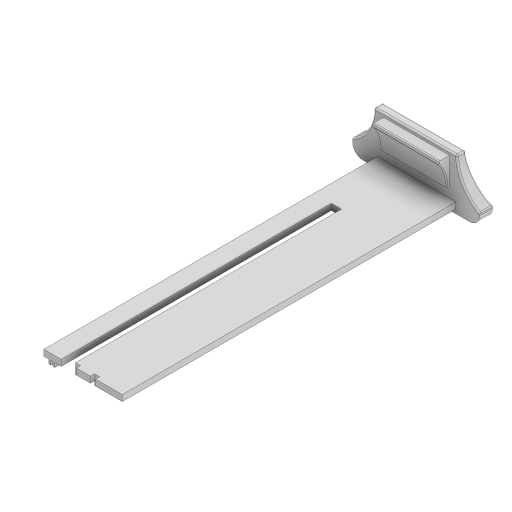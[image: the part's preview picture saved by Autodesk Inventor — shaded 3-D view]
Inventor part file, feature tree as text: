
AUTODESK INVENTOR PART (.ipt)
format: ipt  version: 2024 (Build 280153000, 153)  size: 315,392 bytes
history: native  units: mm
features: extrude x8, sketch x5, fillet x3, chamfer x1
ambient origin geometry x8: Origin, YZ Plane, XZ Plane, XY Plane, X Axis, Y Axis, Z Axis, Center Point
bodies: Solid1 (feature_tree)
feature tree (17):
  sketch  "Sketch1"  dims[d0=38.3mm d1=163.0mm]
  extrude  "Extrusion1"  Depth=163.0mm
  sketch  "Sketch2"  dims[d2=62.0mm d3=6.4mm]
  extrude  "Extrusion2"  Depth=6.4mm
  extrude  "Extrusion3"  Depth=132.0mm
  extrude  "Extrusion4"  Depth=2.5mm
  extrude  "Extrusion6"  Depth=5.0mm
  extrude  "Extrusion7"  Depth=5.0mm
  chamfer  "Chamfer2"  Distance=6.9mm
  extrude  "Extrusion8"  Depth=5.0mm TaperAngle=0.0deg
  extrude  "Extrusion9"  Depth=5.0mm
  fillet  "Fillet6"  Radius=0.5mm
  fillet  "Fillet9"  Radius=34.9mm
  fillet  "Fillet10"  Radius=0.5mm
  sketch  "Sketch4"  dims[d4=11.6mm d6=132.0mm]
  sketch  "Sketch5"  dims[d7=8.5mm d8=2.5mm]
  sketch  "Sketch6"  dims[d9=2.0mm d10=2.5mm d11=2.0mm d12=6.9mm d13=3.0mm d14=0.0mm d15=1.0mm d16=0.5mm d17=34.9mm d18=0.5mm d19=0.5mm d20=1.0mm d21=1.0mm d22=1.0mm d23=2.0mm d24=0.0mm d25=1.0mm d26=10.0mm d27=1.0mm d28=1.0mm d29=2.0mm d30=0.0mm d31=23.0mm d32=2.0mm d33=0.0mm d34=0.0mm d44=1.0mm d45=1.5mm d46=4.0mm d47=0.0mm d48=60.0deg d49=6.0mm d50=10.969655mm d51=120.0deg d52=10.392305mm d53=0.0mm d54=0.0mm d55=18.0mm d56=2.0mm d57=1.22173mm d61=4.9mm d62=32.591mm d63=13.174mm d64=5.0mm d65=0.0mm d66=1.682mm d67=1.231mm d68=0.0mm d69=0.0mm d70=0.5mm d73=0.75mm d74=5.0mm d75=5.0mm d76=1.826mm d39=0.0mm d40=0.0mm d41=0.0mm d42=0.0mm]
